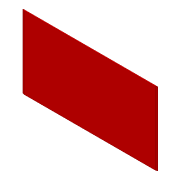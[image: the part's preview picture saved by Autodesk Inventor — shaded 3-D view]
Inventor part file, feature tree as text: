
AUTODESK INVENTOR PART (.ipt)
format: ipt  version: unknown  size: 2,019,328 bytes
history: native  units: in
note: dims shown in document units (in); Inventor stores cm internally (conversion verified against a paired STEP export)
features: chamfer x2, other x2, sketch x2, extrude x1
ambient origin geometry x8: Origin, YZ Plane, XZ Plane, XY Plane, X Axis, Y Axis, Z Axis, Center Point
bodies: Solid1 (feature_tree)
feature tree (7):
  extrude  "Extrusion1"  Depth=88.0in
  chamfer  "Chamfer1"  Distance=0.5in
  chamfer  "Chamfer3"  Distance=0.375in
  other  "Decal1"
  sketch  "Sketch1"  dims[d0=47.5in d1=88.0in d2=0.5in d3=0.0in d4=0.375in d5=0.125in d6=0.5085in]
  sketch  "Sketch2"  dims[d10=0.375in d11=0.125in d12=0.5085in d22=11.0in d23=11.0in d24=82.5701in d25=88.0in d26=2.715in]
  other  "Image1"
